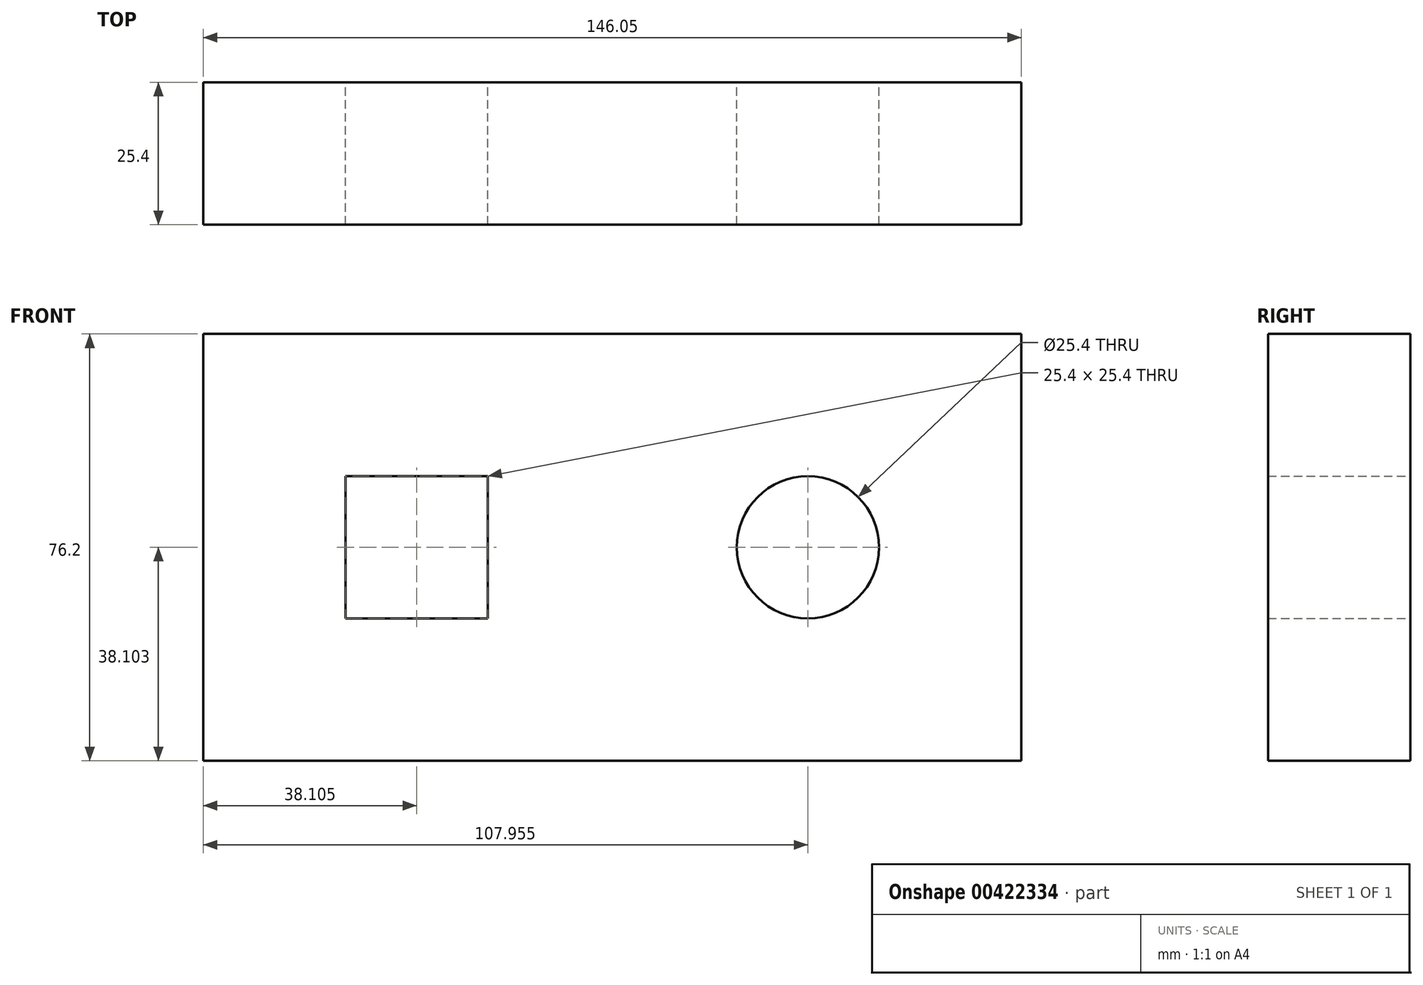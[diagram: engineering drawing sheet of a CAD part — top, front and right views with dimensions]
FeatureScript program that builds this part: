
annotation { "Feature Type Name" : "Feature", "Feature Type Description" : "" }
export const myFeature = defineFeature(function(context is Context, id is Id, definition is map)
    precondition{}
    {
        {
            var Q0;
            Q0=qCreatedBy(makeId("Front.planeOp"),FACE);
            var sketch = newSketch(context, id + "F0", { "sketchPlane" : qUnion([Q0])});
            skLineSegment(sketch, "E0.bottom", {"start": v(83.38, -48.5) * mm, "end": v(-62.67, -48.5) * mm});
            skLineSegment(sketch, "E0.top", {"start": v(83.38, 27.7) * mm, "end": v(-62.67, 27.7) * mm});
            skLineSegment(sketch, "E0.left", {"start": v(83.38, -48.5) * mm, "end": v(83.38, 27.7) * mm});
            skLineSegment(sketch, "E0.right", {"start": v(-62.67, -48.5) * mm, "end": v(-62.67, 27.7) * mm});
            skLineSegment(sketch, "E1.bottom", {"start": v(-11.87, -23.1) * mm, "end": v(-37.27, -23.1) * mm});
            skLineSegment(sketch, "E1.top", {"start": v(-11.87, 2.3) * mm, "end": v(-37.27, 2.3) * mm});
            skLineSegment(sketch, "E1.left", {"start": v(-11.87, -23.1) * mm, "end": v(-11.87, 2.3) * mm});
            skLineSegment(sketch, "E1.right", {"start": v(-37.27, -23.1) * mm, "end": v(-37.27, 2.3) * mm});
            skCircle(sketch, "E2", {"center": v(45.28, -10.4) * mm, "radius": 12.7 * mm});
            skSolve(sketch);
        }
        {
            var Q0;
            Q0 = qSketchRegion(id + "F0", true);
            extrude(context, id + "F1", {"entities" : qUnion([Q0]), "depth" : 25.4 * mm});
        }
    });
